# Revit family: Sanitary_Accessories_DURAVIT-AG_D-Code-Towel-hooks-16x55x16-mm-009904ed
name_source: partatom
category: Generic Models
revit_build: Autodesk Revit 2018 (Build: 20190510_1515(x64)
units: mm (PartAtom-declared; Revit-internal decimal feet)

## family parameters
Can host rebar = No
Cut with Voids When Loaded = No
Host = Face
OmniClass Number = 23.31.25.25
OmniClass Title = Towel Bars
Part Type = Normal
Room Calculation Point = No
Round Connector Dimension = Use Diameter
Shared = No

## types (1)
- D-Code Towel hooks Chrome 16x55x16 mm - 0099041000
    BIMobject category = Bathroom Accessories
    Default Elevation = 1219 mm
    Description = Duravit D-Code Towel hooks Chrome 16x55x16 mm - 0099041000
    Design country = Germany
    ETIM classification = EC010552 | Towel hook
    Edition number = 1
    IFC Classification = Furnishing Element
    Installation instructions = https://pro.duravit.com
    Main material = Duravit - Metal - 10 - Chrome
    Manufacturer = Duravit
    Manufacturer country = Germany
    Manufacturer name = DURAVIT AG
    Masterformat 2014 Code = 10 28 00
    Masterformat 2014 Description = Toilet, Bath, and Laundry Accessories
    Material main = Brass
    Model = D-Code Towel hooks Chrome 16x55x16 mm - 0099041000
    OmniClass Code = 23-31 25 25
    OmniClass Description = Towel Bars
    Product Guid = fc53f7bd-3ed7-4144-a866-2e4cb7684703
    Product SKU = D-Code-Towel-hooks-16x55x16-mm-009904
    Product certification = https://pro.duravit.com
    Product data url = https://bimobject.com
    Product family = Bathtubs & Wellbeing
    Product group = Towel hook
    Product name = D-Code Towel hooks 16x55x16 mm - 009904
    Product url = https://pro.duravit.com
    QR code = https://bimobject.com
    Technical description = https://pro.duravit.com
    UNSPSC Code = 301815
    URL = https://www.duravit.com
    Uniclass 2015 Code = Pr_40_20_76_90
    Uniclass 2015 Name = Towel rails
    Uniformat II Code = E2010
    Uniformat II Description = Fixed Furnishings
    Weight Net (Kg) = 0.1
    Youtube clip = https://pro.duravit.com

## geometry (parser evidence)
native form markers: Sweep x4
no freeform markers — native parametric forms only
